# Revit family: Cabinet_Wenger_UltraStor_54
name_source: partatom
category: Furniture
revit_build: Autodesk Revit 2015 (Build: 20140606_1530(x64)
units: mm (PartAtom-declared; Revit-internal decimal feet)

## types (14) — shared parameters
Assembly Code = E2010200
Cabinet Height = 3' - 2 5/16"
Cabinet Panel Thickness = 0' - 0 3/4"
Construction Details = http://www.arcat.com
Door Height = 1' - 4 25/32"
Green Building-LEED = http://www.arcat.com
Keynote = 12 35 83
Manufacturer = Wenger Corporation
Manufacturer Fax = (507) 455-4258
Manufacturer Website = https://www.wengercorp.com
Product Data = http://www.arcat.com
Revision = R1_2018-04
Sales Information = https://www.wengercorp.com
Shelf Thickness = 0' - 1 1/8"
Specification = http://www.arcat.com
URL = https://www.wengercorp.com
zero-valued in all types: Cost

## per-type parameters (varying)
| type | Cabinet Width | Description | Door Style | Door Width | HasDoors | Installed Depth | Model | Rear Panel Thickness |
| Acoustic Cabinet #54 - No Doors | 2' - 3 1/2" | Wenger Acoustic Cabinet #54 - No Doors | Door_Base : Solid Door | 1' - 0 5/8" | No | 2' - 7 3/4" | #54A | 0' - 3 1/4" |
| Narrow Acoustic Cabinet #54 - No Doors | 1' - 9 1/2" | Wenger Narrow Acoustic Cabinet #54 - No Doors | Door_Base : Solid Door | 0' - 9 5/8" | No | 2' - 7 3/4" | #54NA | 0' - 3 1/4" |
| Acoustic Cabinet #54 - Comp Waterfall Grille Doors | 2' - 3 1/2" | Wenger Acoustic Cabinet #54 - Comp Waterfall Grille Doors | Door_Base : Waterfall | 1' - 0 5/8" | Yes | 2' - 7 3/4" | #54A | 0' - 3 1/4" |
| Acoustic Cabinet #54 - Comp Grille Doors | 2' - 3 1/2" | Wenger Acoustic Cabinet #54 - Comp Grille Doors | Door_Base : Bars | 1' - 0 5/8" | Yes | 2' - 7 3/4" | #54A | 0' - 3 1/4" |
| Narrow Acoustic Cabinet #54 - Comp Waterfall Grille Doors | 1' - 9 1/2" | Wenger Narrow Acoustic Cabinet #54 - Comp Waterfall Grille Doors | Door_Base : Waterfall | 0' - 9 5/8" | Yes | 2' - 7 3/4" | #54NA | 0' - 3 1/4" |
| Narrow Acoustic Cabinet #54 - Comp Grille Doors | 1' - 9 1/2" | Wenger Narrow Acoustic Cabinet #54 - Comp Grille Doors | Door_Base : Bars | 0' - 9 5/8" | Yes | 2' - 7 3/4" | #54NA | 0' - 3 1/4" |
| Narrow UltraStor Cabinet #54 - No Doors | 1' - 9 1/2" | Wenger Narrow Cabinet #54 - No Doors | Door_Base : Solid Door | 0' - 9 5/8" | No | 2' - 5 1/4" | #54N | 0' - 0 3/4" |
| UltraStor Cabinet #54 - No Doors | 2' - 3 1/2" | Wenger UltraStor Cabinet #54 - No Doors | Door_Base : Solid Door | 1' - 0 5/8" | No | 2' - 5 1/4" | #54 | 0' - 0 3/4" |
| UltraStor Cabinet #54 - Comp Grille Doors | 2' - 3 1/2" | Wenger UltraStor Cabinet #54 - Comp Grille Doors | Door_Base : Bars | 1' - 0 5/8" | Yes | 2' - 5 1/4" | #54 | 0' - 0 3/4" |
| Narrow UltraStor Cabinet #54 - Comp Waterfall Grille Doors | 1' - 9 1/2" | Wenger Narrow Cabinet #54 - Comp Waterfall Grille Doors | Door_Base : Waterfall | 0' - 9 5/8" | Yes | 2' - 5 1/4" | #54N | 0' - 0 3/4" |
| Narrow UltraStor Cabinet #54 - Comp Grille Doors | 1' - 9 1/2" | Wenger Narrow Cabinet #54 - Comp Grille Doors | Door_Base : Bars | 0' - 9 5/8" | Yes | 2' - 5 1/4" | #54N | 0' - 0 3/4" |
| Narrow UltraStor Cabinet #54 - Comp Wood Doors | 1' - 9 1/2" | Wenger Narrow Cabinet #54 - Comp Wood Doors | Door_Base : Solid Door | 0' - 9 5/8" | Yes | 2' - 5 1/4" | #54N | 0' - 0 3/4" |
| UltraStor Cabinet #54 - Comp Wood Doors | 2' - 3 1/2" | Wenger UltraStor Cabinet #54 - Comp Wood Doors | Door_Base : Solid Door | 1' - 0 5/8" | Yes | 2' - 5 1/4" | #54 | 0' - 0 3/4" |
| UltraStor Cabinet #54 - Comp Waterfall Grille Doors | 2' - 3 1/2" | Wenger UltraStor Cabinet #54 - Comp Waterfall Grille Doors | Door_Base : Waterfall | 1' - 0 5/8" | Yes | 2' - 5 1/4" | #54 | 0' - 0 3/4" |

## geometry (parser evidence)
native form markers: Blend x20, Sweep x11
no freeform markers — native parametric forms only
